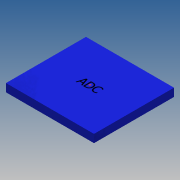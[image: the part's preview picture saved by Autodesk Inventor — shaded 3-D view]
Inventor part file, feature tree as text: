
AUTODESK INVENTOR PART (.ipt)
format: ipt  version: 2016 SP2 (Build 200236200, 236)  size: 86,016 bytes
history: native  units: mm
features: sketch x2, extrude x1
ambient origin geometry x8: Origin, YZ Plane, XZ Plane, XY Plane, X Axis, Y Axis, Z Axis, Center Point
bodies: Solid1 (feature_tree)
feature tree (3):
  extrude  "Extrusion1"  Depth=100.0mm
  sketch  "Sketch2"  dims[d2=10.0mm d3=0.0mm]
  sketch  "Sketch1"  dims[d0=110.0mm d1=100.0mm]
